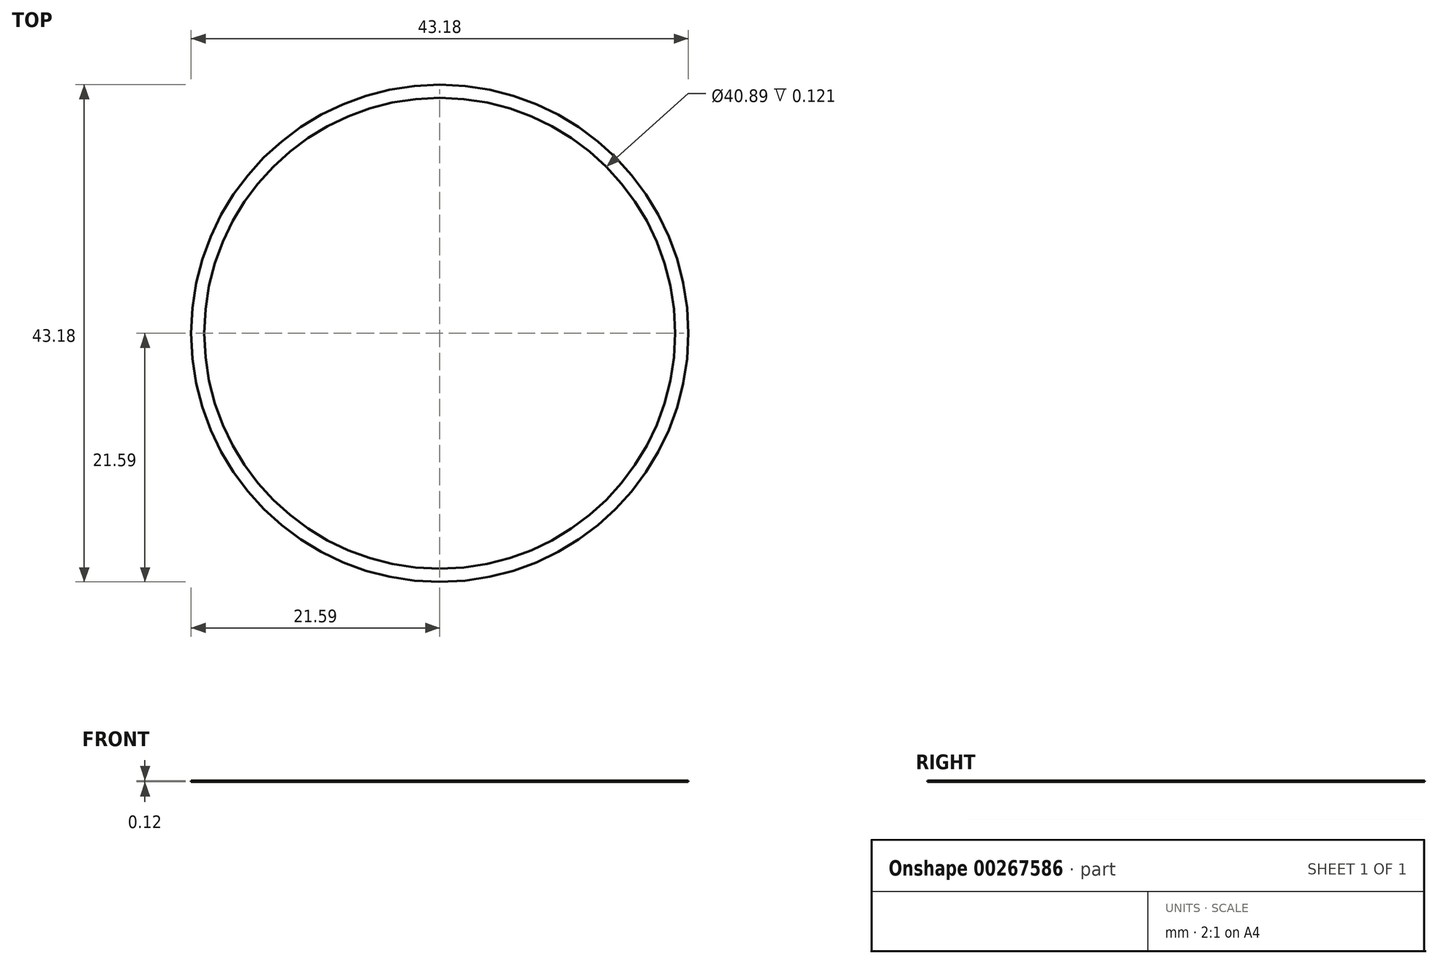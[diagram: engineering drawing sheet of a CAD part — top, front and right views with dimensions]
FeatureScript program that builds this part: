
annotation { "Feature Type Name" : "Feature", "Feature Type Description" : "" }
export const myFeature = defineFeature(function(context is Context, id is Id, definition is map)
    precondition{}
    {
        {
            var Q0;
            Q0=qCreatedBy(makeId("Top.planeOp"),FACE);
            var sketch = newSketch(context, id + "F0", { "sketchPlane" : qUnion([Q0])});
            skCircle(sketch, "E0", {"center": v(0, 0) * mm, "radius": 20.45 * mm});
            skCircle(sketch, "E1", {"center": v(0, 0) * mm, "radius": 21.59 * mm});
            skSolve(sketch);
        }
        {
            var Q0;
            Q0 = qSketchRegion(id + "F0", true);
            extrude(context, id + "F1", {"entities" : qUnion([Q0]), "depth" : 6.12 / 50.8 * mm});
        }
    });
